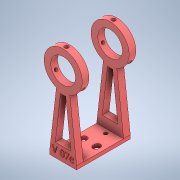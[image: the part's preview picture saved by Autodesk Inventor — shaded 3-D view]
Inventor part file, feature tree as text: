
AUTODESK INVENTOR PART (.ipt)
format: ipt  version: 2021.1 (Build 251245000, 245)  size: 407,040 bytes
history: native  units: in
note: dims shown in document units (in); Inventor stores cm internally (conversion verified against a paired STEP export)
features: sketch x8, extrude x7, plane x2, hole x2, pattern_circular x1, mirror x1
ambient origin geometry x8: Origin, YZ Plane, XZ Plane, XY Plane, X Axis, Y Axis, Z Axis, Center Point
bodies: Solid1 (feature_tree)
feature tree (21):
  extrude  "Extrusion1"  Depth=0.75in
  extrude  "Extrusion2"  Depth=3.0in TaperAngle=0.0deg
  plane  "Work Plane1"
  extrude  "Extrusion4"  Depth=1.375in
  plane  "Work Plane2"
  sketch  "Sketch6"  dims[d9=0.0in d10=0.0in d15=1.375in]
  hole  "Hole2"  [1 undecoded]
  extrude  "Extrusion7"  Depth=0.375in TaperAngle=0.0deg
  hole  "Hole1"  [1 undecoded]
  extrude  "Extrusion8"  TaperAngle=60.0deg  [1 undecoded]
  pattern_circular  "Circular Pattern2"  Angle=60.0deg  [1 undecoded]
  mirror  "Mirror2"
  extrude  "TextIdentifier"  Depth=0.375in
  extrude  "Extrusion10"  TaperAngle=60.0deg  [1 undecoded]
  sketch  "Sketch1"  dims[d0=6.0in d1=0.75in]
  sketch  "Sketch5"  dims[d2=0.5in d3=3.0in d4=0.0in]
  sketch  "Sketch20"  dims[d16=0.375in d17=4.725in]
  sketch  "Sketch22"  dims[d18=0.375in d19=0.375in d20=0.0in]
  sketch  "Sketch23"  dims[d51=0.0039in d53=60.0deg]
  sketch  "Sketch24"  dims[d72=0.0039in d74=60.0deg]
  sketch  "Sketch25"  dims[d93=0.0039in d95=60.0deg d114=0.0039in d116=60.0deg d135=0.0039in d137=60.0deg d156=0.0039in d158=60.0deg d168=0.125in d169=0.0in d173=0.25in d174=0.25in d175=0.201in d176=0.38in d177=0.375in d178=0.125in d179=0.5635in d180=1.0in d181=0.8108in d183=0.625in d185=0.05in d186=0.0in d187=0.0in d188=0.177in d189=0.75in d190=0.221in d191=0.25in d192=0.5635in d193=0.4in d194=0.8108in d195=1.1811in d196=360.0deg d198=0.4in d199=0.05in d200=0.0in d202=0.325in d204=0.1in d211=0.75in d212=0.25in d213=0.0in d214=0.0in]
note: 5 required parameter values undecoded (feature->parameter linkage not recoverable at this tier; creation-order binding heuristic only, values carry confidence <= 0.55)
